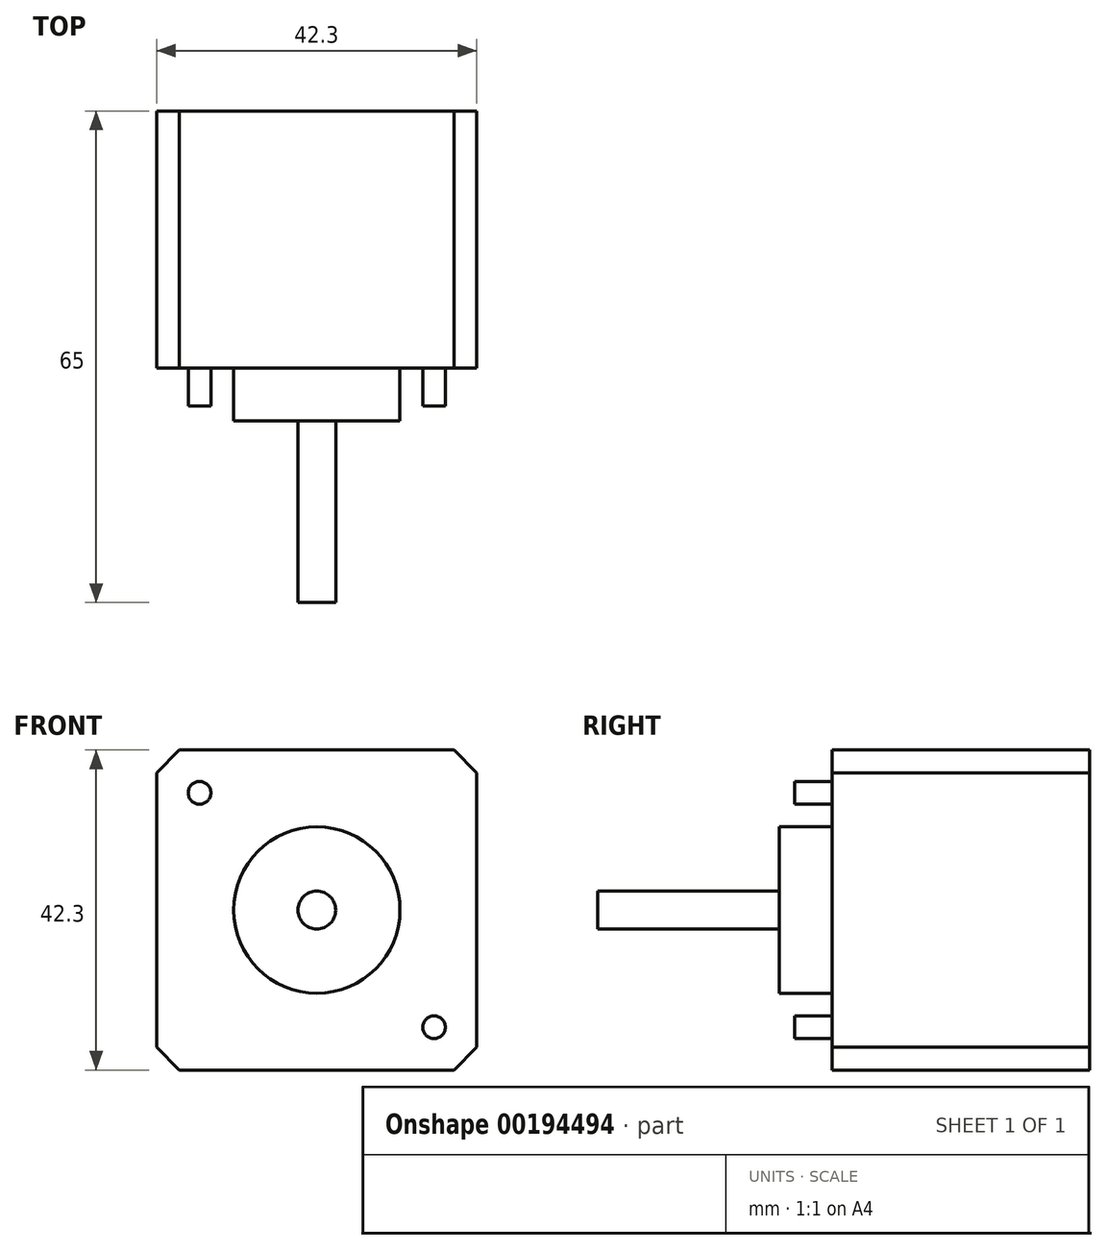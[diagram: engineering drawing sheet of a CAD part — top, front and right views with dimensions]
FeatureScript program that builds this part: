
annotation { "Feature Type Name" : "Feature", "Feature Type Description" : "" }
export const myFeature = defineFeature(function(context is Context, id is Id, definition is map)
    precondition{}
    {
        {
            var Q0;
            Q0=qCreatedBy(makeId("Front.planeOp"),FACE);
            var sketch = newSketch(context, id + "F0", { "sketchPlane" : qUnion([Q0])});
            skPoint(sketch, "E0.middle", {"position": v(0, 0) * mm});
            skLineSegment(sketch, "E1", {"start": v(18.15, 21.15) * mm, "end": v(21.15, 18.15) * mm});
            skLineSegment(sketch, "E2.MirrorCS", {"start": v(-21.15, -18.15) * mm, "end": v(-18.15, -21.15) * mm});
            skLineSegment(sketch, "E3", {"start": v(-21.15, 18.15) * mm, "end": v(-18.15, 21.15) * mm});
            skLineSegment(sketch, "E4.MirrorCS", {"start": v(18.15, -21.15) * mm, "end": v(21.15, -18.15) * mm});
            skLineSegment(sketch, "E5", {"start": v(-21.15, -18.15) * mm, "end": v(-21.15, 18.15) * mm});
            skLineSegment(sketch, "E6", {"start": v(-18.15, 21.15) * mm, "end": v(18.15, 21.15) * mm});
            skLineSegment(sketch, "E7", {"start": v(21.15, 18.15) * mm, "end": v(21.15, -18.15) * mm});
            skLineSegment(sketch, "E8", {"start": v(18.15, -21.15) * mm, "end": v(-18.15, -21.15) * mm});
            skSolve(sketch);
        }
        {
            var Q0;
            Q0=makeQuery(id+"F0.imprint","IMPRINT",FACE,{"disambiguationData":[TD([[makeQuery(id+"F0.imprint","IMPRINT",EDGE,{"derivedFrom":sQuery(id+"F0.wireOp",EDGE,"E1")}),-1.0]])]});
            extrude(context, id + "F1", {"entities" : qUnion([Q0]), "depth" : 39 * mm, "offsetDistance" : 25.4 * mm});
        }
        {
            var Q0;
            Q0=makeQuery(id+"F1.opExtrude","CAP_FACE",FACE,{"disambiguationData":[OSD([sQuery(id+"F0.wireOp",EDGE,"E1"),sQuery(id+"F0.wireOp",EDGE,"E2.MirrorCS"),sQuery(id+"F0.wireOp",EDGE,"E3"),sQuery(id+"F0.wireOp",EDGE,"E4.MirrorCS"),sQuery(id+"F0.wireOp",EDGE,"E5"),sQuery(id+"F0.wireOp",EDGE,"E6"),sQuery(id+"F0.wireOp",EDGE,"E7"),sQuery(id+"F0.wireOp",EDGE,"E8")])],"isStart":false});
            var sketch = newSketch(context, id + "F2", { "sketchPlane" : qUnion([Q0])});
            skCircle(sketch, "E9", {"center": v(0, 0) * mm, "radius": 11 * mm});
            skLineSegment(sketch, "E10", {"start": v(0, 0) * mm, "end": v(0, -15.5) * mm});
            skLineSegment(sketch, "E11", {"start": v(0, 0) * mm, "end": v(15.5, 0) * mm});
            skLineSegment(sketch, "E12.MirrorCS", {"start": v(0, 0) * mm, "end": v(-15.5, 0) * mm});
            skLineSegment(sketch, "E13.MirrorCS", {"start": v(0, 0) * mm, "end": v(0, 15.5) * mm});
            skLineSegment(sketch, "E14", {"start": v(0, 15.5) * mm, "end": v(15.5, 15.5) * mm});
            skLineSegment(sketch, "E15", {"start": v(15.5, 15.5) * mm, "end": v(15.5, 0) * mm});
            skLineSegment(sketch, "E16", {"start": v(15.5, -15.5) * mm, "end": v(15.5, 0) * mm});
            skLineSegment(sketch, "E17", {"start": v(15.5, -15.5) * mm, "end": v(0, -15.5) * mm});
            skLineSegment(sketch, "E18", {"start": v(-15.5, -15.5) * mm, "end": v(0, -15.5) * mm});
            skLineSegment(sketch, "E19", {"start": v(-15.5, -15.5) * mm, "end": v(-15.5, 0) * mm});
            skLineSegment(sketch, "E20", {"start": v(-15.5, 15.5) * mm, "end": v(-15.5, 0) * mm});
            skLineSegment(sketch, "E21", {"start": v(-15.5, 15.5) * mm, "end": v(0, 15.5) * mm});
            skCircle(sketch, "E22", {"center": v(15.5, 15.5) * mm, "radius": 1.5 * mm});
            skCircle(sketch, "E23", {"center": v(15.5, -15.5) * mm, "radius": 1.5 * mm});
            skCircle(sketch, "E24", {"center": v(-15.5, -15.5) * mm, "radius": 1.5 * mm});
            skCircle(sketch, "E25", {"center": v(-15.5, 15.5) * mm, "radius": 1.5 * mm});
            skSolve(sketch);
        }
        {
            var Q0;
            {var subQ0=sQuery(id+"F2.wireOp",EDGE,"E12.MirrorCS");var subQ1=sQuery(id+"F2.wireOp",EDGE,"E9");var subQ2=makeQuery(id+"F2.imprint","INTERSECT",VERTEX,{"derivedFrom":[subQ1,subQ0]});Q0=makeQuery(id+"F2.imprint","IMPRINT",FACE,{"disambiguationData":[TD([[makeQuery(id+"F2.imprint","IMPRINT",EDGE,{"disambiguationData":[TD([[subQ2,-1.0]])],"derivedFrom":subQ1}),1.0]])]});}
            var Q1;
            {var subQ0=sQuery(id+"F2.wireOp",EDGE,"E13.MirrorCS");var subQ1=sQuery(id+"F2.wireOp",EDGE,"E9");var subQ2=makeQuery(id+"F2.imprint","INTERSECT",VERTEX,{"derivedFrom":[subQ1,subQ0]});Q1=makeQuery(id+"F2.imprint","IMPRINT",FACE,{"disambiguationData":[TD([[makeQuery(id+"F2.imprint","IMPRINT",EDGE,{"disambiguationData":[TD([[subQ2,-1.0]])],"derivedFrom":subQ1}),1.0]])]});}
            var Q2;
            {var subQ0=sQuery(id+"F2.wireOp",EDGE,"E13.MirrorCS");var subQ1=sQuery(id+"F2.wireOp",EDGE,"E9");var subQ2=makeQuery(id+"F2.imprint","INTERSECT",VERTEX,{"derivedFrom":[subQ1,subQ0]});Q2=makeQuery(id+"F2.imprint","IMPRINT",FACE,{"disambiguationData":[TD([[makeQuery(id+"F2.imprint","IMPRINT",EDGE,{"disambiguationData":[TD([[subQ2,1.0]])],"derivedFrom":subQ1}),1.0]])]});}
            var Q3;
            {var subQ0=sQuery(id+"F2.wireOp",EDGE,"E11");var subQ1=sQuery(id+"F2.wireOp",EDGE,"E9");var subQ2=makeQuery(id+"F2.imprint","INTERSECT",VERTEX,{"derivedFrom":[subQ1,subQ0]});Q3=makeQuery(id+"F2.imprint","IMPRINT",FACE,{"disambiguationData":[TD([[makeQuery(id+"F2.imprint","IMPRINT",EDGE,{"disambiguationData":[TD([[subQ2,1.0]])],"derivedFrom":subQ1}),1.0]])]});}
            extrude(context, id + "F3", {"entities" : qUnion([Q0, Q1, Q2, Q3]), "operationType" : NewBodyOperationType.ADD, "depth" : 2 * mm, "offsetDistance" : 25.4 * mm});
        }
        {
            var Q0;
            Q0=makeQuery(id+"F3.opExtrude","CAP_FACE",FACE,{"disambiguationData":[OSD([sQuery(id+"F2.wireOp",EDGE,"E9")])],"isStart":false});
            var sketch = newSketch(context, id + "F4", { "sketchPlane" : qUnion([Q0])});
            skCircle(sketch, "E26", {"center": v(0, 0) * mm, "radius": 2.5 * mm});
            skSolve(sketch);
        }
        {
            var Q0;
            Q0 = qSketchRegion(id + "F4", true);
            var Q1;
            Q1=makeQuery(id+"F4.imprint","IMPRINT",FACE,{"disambiguationData":[TD([[makeQuery(id+"F4.imprint","IMPRINT",EDGE,{"derivedFrom":sQuery(id+"F4.wireOp",EDGE,"E26")}),1.0]])]});
            extrude(context, id + "F5", {"entities" : qUnion([Q0, Q1]), "operationType" : NewBodyOperationType.ADD, "depth" : 24 * mm, "offsetDistance" : 25.4 * mm});
        }
        {
            var Q0;
            Q0=makeQuery(id+"F1.opExtrude","CAP_FACE",FACE,{"disambiguationData":[OSD([sQuery(id+"F0.wireOp",EDGE,"E1"),sQuery(id+"F0.wireOp",EDGE,"E2.MirrorCS"),sQuery(id+"F0.wireOp",EDGE,"E3"),sQuery(id+"F0.wireOp",EDGE,"E4.MirrorCS"),sQuery(id+"F0.wireOp",EDGE,"E5"),sQuery(id+"F0.wireOp",EDGE,"E6"),sQuery(id+"F0.wireOp",EDGE,"E7"),sQuery(id+"F0.wireOp",EDGE,"E8")])],"isStart":false});
            var sketch = newSketch(context, id + "F6", { "sketchPlane" : qUnion([Q0])});
            skLineSegment(sketch, "E27", {"start": v(0, 0) * mm, "end": v(0, 15.5) * mm});
            skLineSegment(sketch, "E28", {"start": v(0, 15.5) * mm, "end": v(15.5, 15.5) * mm});
            skCircle(sketch, "E29", {"center": v(15.5, 15.5) * mm, "radius": 1.5 * mm});
            skCircle(sketch, "E30.MirrorC", {"center": v(15.5, -15.5) * mm, "radius": 1.5 * mm});
            skCircle(sketch, "E31.MirrorC", {"center": v(-15.5, 15.5) * mm, "radius": 1.5 * mm});
            skCircle(sketch, "E32.MirrorC", {"center": v(-15.5, -15.5) * mm, "radius": 1.5 * mm});
            skSolve(sketch);
        }
        {
            var Q0;
            Q0=makeQuery(id+"F6.imprint","IMPRINT",FACE,{"disambiguationData":[TD([[makeQuery(id+"F6.imprint","IMPRINT",EDGE,{"derivedFrom":sQuery(id+"F6.wireOp",EDGE,"E31.MirrorC")}),-1.0]])]});
            var Q1;
            Q1=makeQuery(id+"F6.imprint","IMPRINT",FACE,{"disambiguationData":[TD([[makeQuery(id+"F6.imprint","IMPRINT",EDGE,{"derivedFrom":sQuery(id+"F6.wireOp",EDGE,"E29")}),1.0]])]});
            var Q2;
            Q2=makeQuery(id+"F6.imprint","IMPRINT",FACE,{"disambiguationData":[TD([[makeQuery(id+"F6.imprint","IMPRINT",EDGE,{"derivedFrom":sQuery(id+"F6.wireOp",EDGE,"E30.MirrorC")}),-1.0]])]});
            var Q3;
            Q3=makeQuery(id+"F6.imprint","IMPRINT",FACE,{"disambiguationData":[TD([[makeQuery(id+"F6.imprint","IMPRINT",EDGE,{"derivedFrom":sQuery(id+"F6.wireOp",EDGE,"E32.MirrorC")}),1.0]])]});
            extrude(context, id + "F7", {"entities" : qUnion([Q0, Q1, Q2, Q3]), "operationType" : NewBodyOperationType.REMOVE, "oppositeDirection" : true, "depth" : 5 * mm, "offsetDistance" : 25.4 * mm});
        }
    });
